# Revit family: LCOM
name_source: partatom
category: Lighting Fixtures
units: mm (PartAtom-declared; Revit-internal decimal feet)

## family parameters
Cut with Voids When Loaded = No
Host = Face
Light Source = Yes
OmniClass Number = 23.80.70.11.14.11
OmniClass Title = Downlights
Part Type = Normal
Room Calculation Point = No
Round Connector Dimension = Use Diameter
Shared = No

## types (7) — shared parameters
Color Filter = 16777215
Default Elevation = 4' - 0"
Description = Commercial-grade, LED strip luminaire
Dimming Lamp Color Temperature Shift = <None>
Lamp = LED
Manufacturer = Visioneering By Viscor
Model = LCOM
Tilt Angle = -90.00°
URL = https://www.viscor.com
Voltage = 120 V
Width = 0' - 2 13/16"

## per-type parameters (varying)
| type | Apparent Load | Assembly Code | Emit from Line Length | Housing Finish | Lamp Wattage | Length | Photometric Web File |
| LCOM48-LED840K030LUNV | 21 VA |  | 3' - 9 3/16" | <By Category> | 21 VA | 3' - 9 3/16" | LCOM48-LED840K030LUNV-G001211.IES |
| LCOM24-LED840K022LUNV | 17 VA | D5020200 | 1' - 11 1/8" | <By Category> | 17 VA | 1' - 11 1/8" | LCOM24-LED840K022LUNV-G001265.IES |
| LCOM96-LED840K088LUNV | 75 VA |  | 7' - 6 1/4" | <By Category> | 75 VA | 7' - 6 1/4" | LCOM96-LED840K088LUNV.ies |
| LCOM24-LED840K035LUNV | 26 VA |  | 1' - 11 1/8" | <By Category> | 26 VA | 1' - 11 1/8" | LCOM24-LED840K035LUNV-G001268.IES |
| LCOM48-LED840K044LUNV | 34 VA |  | 3' - 9 3/16" | <By Category> | 34 VA | 3' - 9 3/16" | LCOM48-LED840K030LUNV-G001211.IES |
| LCOM48-LED840K070LUNV | 52 VA |  | 7' - 6 1/4" | <By Category> | 52 VA | 7' - 6 1/4" | LCOM96-LED840K088LUNV.ies |
| LCOM96-LED840K140LUNV | 104 VA |  | 7' - 6 1/4" | Metal - Viscor - White | 104 VA | 7' - 6 1/4" | LCOM96-LED840K088LUNV.ies |

## geometry (parser evidence)
native form markers: Sweep x2
no freeform markers — native parametric forms only
